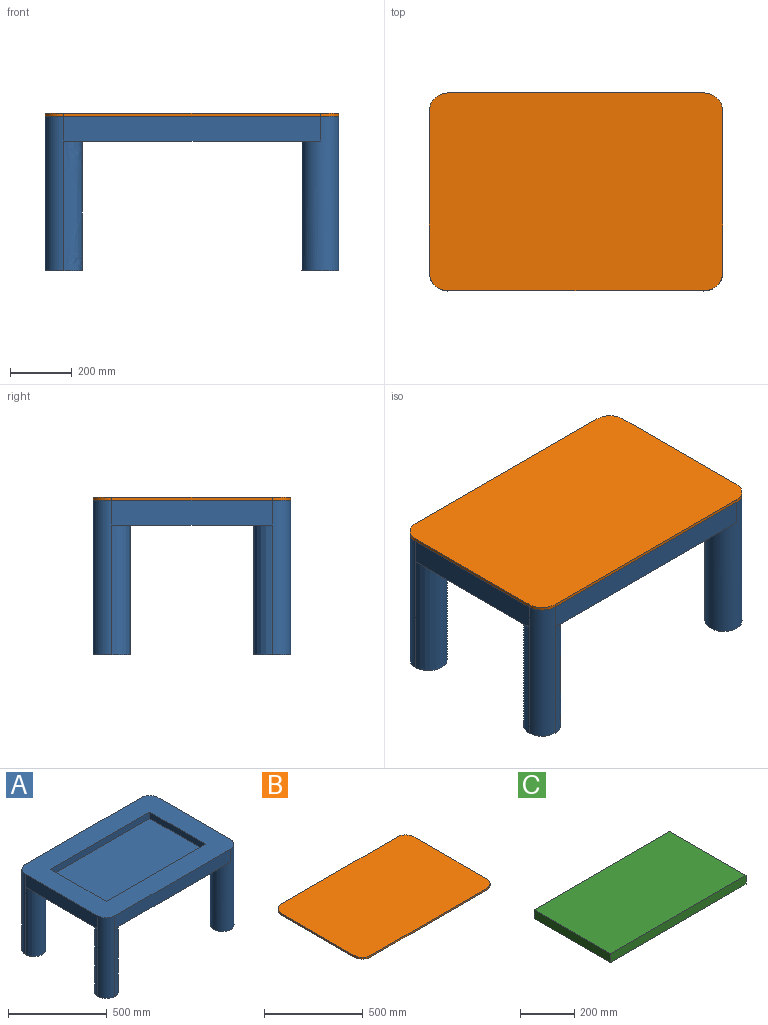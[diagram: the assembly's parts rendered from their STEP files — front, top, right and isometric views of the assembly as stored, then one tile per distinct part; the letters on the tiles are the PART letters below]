
ASSEMBLY  parts=3 mates=2
PART A: 21 faces, bbox 950x640x500 mm
  f0: plane 711.2x40mm, normal (0,-1,0), area 28448mm2, adj f1,f11,f12,f14
  f1: plane 398.78x40mm, normal (-1,0,0), area 15951.2mm2, adj f0,f2,f12,f14
  f2: plane 711.2x40mm, normal (0,1,0), area 28448mm2, adj f1,f11,f12,f14
  f3: plane 520x80mm, normal (1,0,0), area 41600mm2, adj f4,f10,f12,f13
  f4: cylinder r=60mm len=500mm, axis (0,0,-1), area 165876.1mm2, adj f3,f5,f12,f13,f16
  f5: plane 830x80mm, normal (0,1,0), area 66400mm2, adj f4,f6,f12,f13
  f6: cylinder r=60mm len=500mm, axis (0,0,-1), area 47123.9mm2, adj f5,f7,f12,f19,f20
  f7: plane 520x80mm, normal (-1,0,0), area 41600mm2, adj f6,f8,f12,f13
  f8: cylinder r=60mm len=500mm, axis (0,0,-1), area 47123.9mm2, adj f7,f9,f12,f17,f18
  f9: plane 830x80mm, normal (0,-1,0), area 66400mm2, adj f8,f10,f12,f13
  f10: cylinder r=60mm len=500mm, axis (0,0,-1), area 165876.1mm2, adj f3,f9,f12,f13,f15
  f11: plane 398.78x40mm, normal (1,0,0), area 15951.2mm2, adj f0,f2,f12,f14
  f12: plane 950x640mm, normal (0,0,1), area 321297.4mm2, adj f0,f1,f2,f3,f4,f5,f6,f7
  f13: plane 950x640mm, normal (0,0,-1), area 559671mm2, adj f3,f4,f5,f7,f9,f10,f17,f19
  f14: plane 711.2x398.78mm, normal (0,0,1), area 283612.3mm2, adj f0,f1,f2,f11
  f15: plane 120x120mm, normal (0,0,-1), area 11309.7mm2, adj f10
  f16: plane 120x120mm, normal (0,0,-1), area 11309.7mm2, adj f4
  f17: extruded ~420x119.93mm, area 118758.2mm2, adj f8,f13,f18
  f18: plane 120.01x120.01mm, normal (0,0,-1), area 11309.3mm2, adj f8,f17
  f19: extruded ~420x119.93mm, area 118758.6mm2, adj f6,f13,f20
  f20: plane 120.01x120.01mm, normal (0,0,-1), area 11309.8mm2, adj f6,f19
PART B: 10 faces, bbox 950x640x10 mm
  f0: plane 520x10mm, normal (1,0,0), area 5200mm2, adj f1,f7,f8,f9
  f1: cylinder r=60mm len=60mm, axis (0,0,-1), area 942.5mm2, adj f0,f2,f8,f9
  f2: plane 830x10mm, normal (0,1,0), area 8300mm2, adj f1,f3,f8,f9
  f3: cylinder r=60mm len=60mm, axis (0,0,-1), area 942.5mm2, adj f2,f4,f8,f9
  f4: plane 520x10mm, normal (-1,0,0), area 5200mm2, adj f3,f5,f8,f9
  f5: cylinder r=60mm len=60mm, axis (0,0,-1), area 942.5mm2, adj f4,f6,f8,f9
  f6: plane 830x10mm, normal (0,-1,0), area 8300mm2, adj f5,f7,f8,f9
  f7: cylinder r=60mm len=60mm, axis (0,0,-1), area 942.5mm2, adj f0,f6,f8,f9
  f8: plane 950x640mm, normal (0,0,1), area 604909.7mm2, adj f0,f1,f2,f3,f4,f5,f6,f7
  f9: plane 950x640mm, normal (0,0,-1), area 604909.7mm2, adj f0,f1,f2,f3,f4,f5,f6,f7
PART C: 6 faces, bbox 711.2x398.8x40 mm
  f0: plane 398.78x40mm, normal (1,0,0), area 15951.2mm2, adj f1,f3,f4,f5
  f1: plane 711.2x40mm, normal (0,1,0), area 28448mm2, adj f0,f2,f4,f5
  f2: plane 398.78x40mm, normal (-1,0,0), area 15951.2mm2, adj f1,f3,f4,f5
  f3: plane 711.2x40mm, normal (0,-1,0), area 28448mm2, adj f0,f2,f4,f5
  f4: plane 711.2x398.78mm, normal (0,0,1), area 283612.3mm2, adj f0,f1,f2,f3
  f5: plane 711.2x398.78mm, normal (0,0,-1), area 283612.3mm2, adj f0,f1,f2,f3
PLACE A t=(-36.71,-121.54,148.49)mm
PLACE B t=(-47.81,-121.54,228.49)mm
PLACE C t=(-36.71,-121.54,188.49)mm
MATE fastened C.f5 <-> A.f14  axis (0,0,-1) through (-36.71,-121.54,188.49)mm
MATE fastened B.f9 <-> C.f4  axis (0,0,-1) through (-36.71,-121.54,228.49)mm
